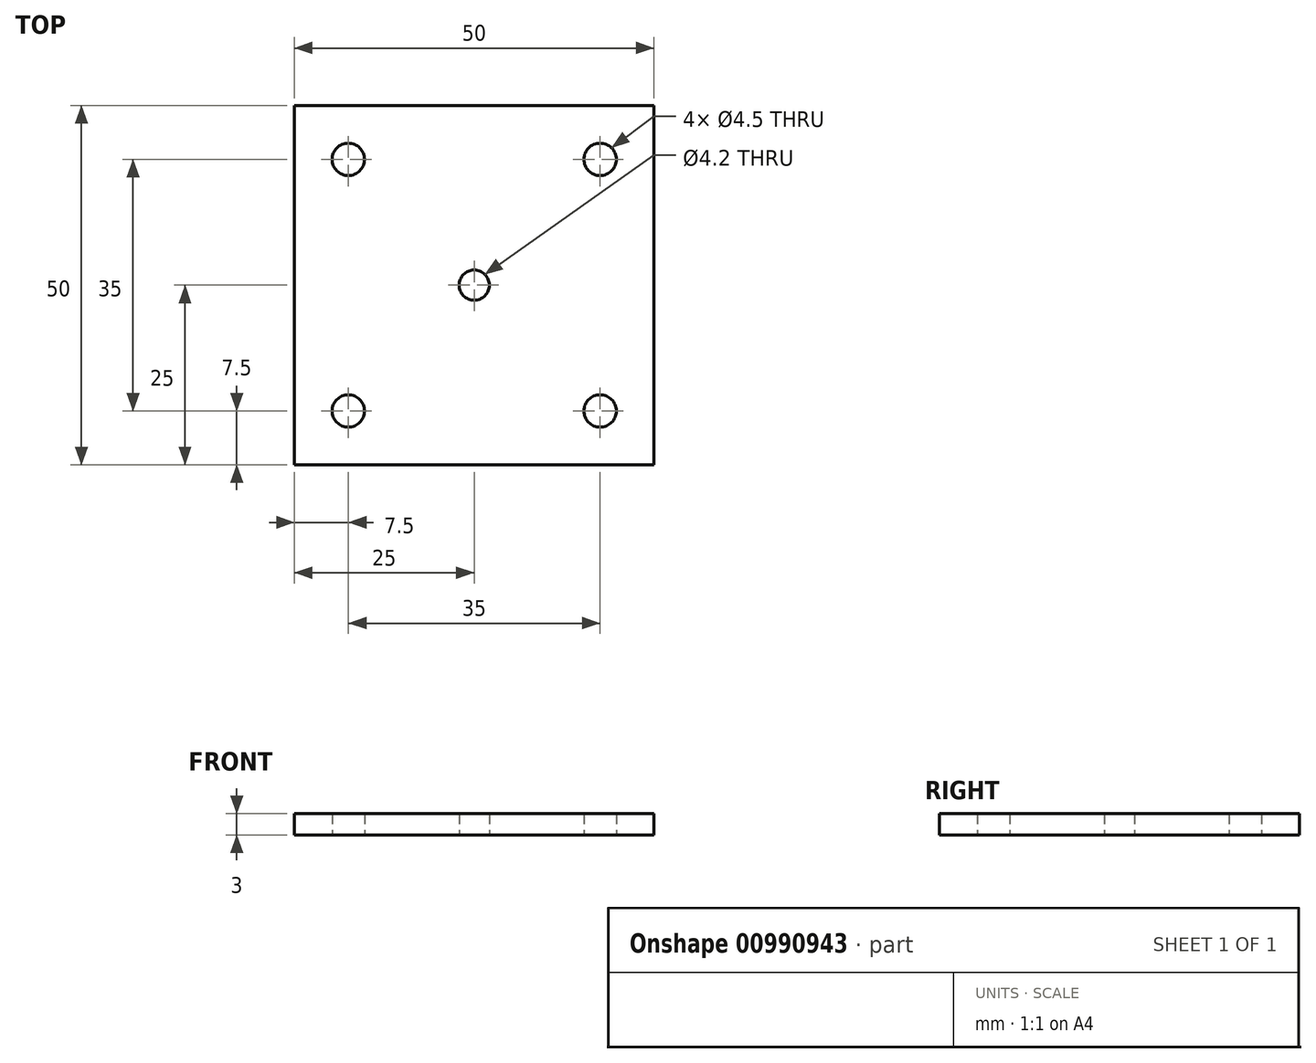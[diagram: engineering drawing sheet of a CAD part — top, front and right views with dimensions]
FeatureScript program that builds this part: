
annotation { "Feature Type Name" : "Feature", "Feature Type Description" : "" }
export const myFeature = defineFeature(function(context is Context, id is Id, definition is map)
    precondition{}
    {
        {
            var Q0;
            Q0=qCreatedBy(makeId("Top.planeOp"),FACE);
            var sketch = newSketch(context, id + "F0", { "sketchPlane" : qUnion([Q0])});
            skLineSegment(sketch, "E0.bottom", {"start": v(25, -25) * mm, "end": v(-25, -25) * mm});
            skLineSegment(sketch, "E0.top", {"start": v(25, 25) * mm, "end": v(-25, 25) * mm});
            skLineSegment(sketch, "E0.left", {"start": v(25, -25) * mm, "end": v(25, 25) * mm});
            skLineSegment(sketch, "E0.right", {"start": v(-25, -25) * mm, "end": v(-25, 25) * mm});
            skLineSegment(sketch, "E1", {"start": v(-25, 17.5) * mm, "end": v(25, 17.5) * mm, "construction": true});
            skLineSegment(sketch, "E2", {"start": v(-25, -17.5) * mm, "end": v(25, -17.5) * mm, "construction": true});
            skLineSegment(sketch, "E3", {"start": v(-17.5, -25) * mm, "end": v(-17.5, 25) * mm, "construction": true});
            skLineSegment(sketch, "E4", {"start": v(17.5, 25) * mm, "end": v(17.5, -25) * mm, "construction": true});
            skLineSegment(sketch, "E5", {"start": v(0, 25) * mm, "end": v(0, -25) * mm, "construction": true});
            skCircle(sketch, "E6", {"center": v(-17.5, 17.5) * mm, "radius": 2 * mm});
            skCircle(sketch, "E7", {"center": v(17.5, 17.5) * mm, "radius": 2 * mm});
            skCircle(sketch, "E8", {"center": v(-17.5, -17.5) * mm, "radius": 2 * mm});
            skCircle(sketch, "E9", {"center": v(17.5, -17.5) * mm, "radius": 2 * mm});
            skLineSegment(sketch, "E10", {"start": v(-25, 0) * mm, "end": v(25, 0) * mm, "construction": true});
            skCircle(sketch, "E11", {"center": v(0, 0) * mm, "radius": 2.1 * mm});
            skSolve(sketch);
        }
        {
            var Q0;
            Q0=makeQuery(id+"F0.imprint","IMPRINT",FACE,{"disambiguationData":[TD([[makeQuery(id+"F0.imprint","IMPRINT",EDGE,{"derivedFrom":sQuery(id+"F0.wireOp",EDGE,"E0.bottom")}),-1.0]])]});
            var Q1;
            Q1=makeQuery(id+"F0.imprint","IMPRINT",FACE,{"disambiguationData":[TD([[makeQuery(id+"F0.imprint","IMPRINT",EDGE,{"derivedFrom":sQuery(id+"F0.wireOp",EDGE,"b2b6f342-489f-4b79-9c51-9a3396d51b60")}),-1.0]])]});
            extrude(context, id + "F1", {"entities" : qUnion([Q0, Q1]), "depth" : 3 * mm, "offsetDistance" : 25 * mm});
        }
        {
            var Q0;
            Q0=sQuery(id+"F0.wireOp",VERTEX,"E8.center");
            var Q1;
            Q1=sQuery(id+"F0.wireOp",VERTEX,"E6.center");
            var Q2;
            Q2=sQuery(id+"F0.wireOp",VERTEX,"E7.center");
            var Q3;
            Q3=sQuery(id+"F0.wireOp",VERTEX,"E9.center");
            var Q4;
            Q4=makeQuery(id+"F1.opExtrude","SWEPT_BODY",BODY,{"disambiguationData":[OSD([sQuery(id+"F0.wireOp",EDGE,"E0.bottom"),sQuery(id+"F0.wireOp",EDGE,"E0.top"),sQuery(id+"F0.wireOp",EDGE,"E0.left"),sQuery(id+"F0.wireOp",EDGE,"E0.right"),sQuery(id+"F0.wireOp",EDGE,"b2b6f342-489f-4b79-9c51-9a3396d51b60"),sQuery(id+"F0.wireOp",EDGE,"6bb16164-fd4e-412d-b9f2-a15617f291ff"),sQuery(id+"F0.wireOp",EDGE,"565172ef-18f3-4f28-ad87-840b49099790"),sQuery(id+"F0.wireOp",EDGE,"a44713ad-60b0-4b4b-bcf8-4b677cbb409a"),sQuery(id+"F0.wireOp",EDGE,"E6"),sQuery(id+"F0.wireOp",EDGE,"E7"),sQuery(id+"F0.wireOp",EDGE,"E8"),sQuery(id+"F0.wireOp",EDGE,"E9")])]});
            hole(context, id + "F2", {"style" : HoleStyle.SIMPLE, "endStyle" : HoleEndStyle.THROUGH, "oppositeDirection" : true, "standardTappedOrClearance" : lookupTablePath({ "fit" : "Normal", "standard" : "ISO", "size" : "M4", "type" : "Clearance" }), "standardBlindInLast" : lookupTablePath({ "fit" : "Normal", "standard" : "ISO", "engagement" : "75%", "pitch" : "0.7 mm", "size" : "M4", "type" : "Clearance & tapped" }), "holeDiameter" : 4.5 * mm, "majorDiameter" : 5 * mm, "isTappedThrough" : true, "tappedDepth" : 12 * mm, "tapClearance" : 3, "locations" : qUnion([Q0, Q1, Q2, Q3]), "scope" : qUnion([Q4])});
        }
    });
